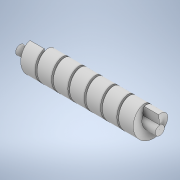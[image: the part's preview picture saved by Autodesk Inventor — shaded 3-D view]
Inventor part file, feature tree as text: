
AUTODESK INVENTOR PART (.ipt)
format: ipt  version: 2021 (Build 250183000, 183)  size: 202,240 bytes
history: native  units: in
note: dims shown in document units (in); Inventor stores cm internally (conversion verified against a paired STEP export)
features: sketch x2, helix x1, extrude x1
ambient origin geometry x8: Origin, YZ Plane, XZ Plane, XY Plane, X Axis, Y Axis, Z Axis, Center Point
bodies: Solid1 (feature_tree)
feature tree (4):
  helix  "Coil1"  [1 undecoded]
  extrude  "Extrusion1"  Depth=2.7559in
  sketch  "Sketch1"  dims[d1=3.937in d2=2.7559in]
  sketch  "Sketch2"  dims[d3=2.7559in d4=3.5433in d5=0.3937in d6=2.7559in d7=0.0in d8=90.0deg d9=90.0deg d10=0.0in d11=0.0in d12=1.9685in d13=30.315in d14=0.0in]
note: 1 required parameter value undecoded (feature->parameter linkage not recoverable at this tier; creation-order binding heuristic only, values carry confidence <= 0.55)
